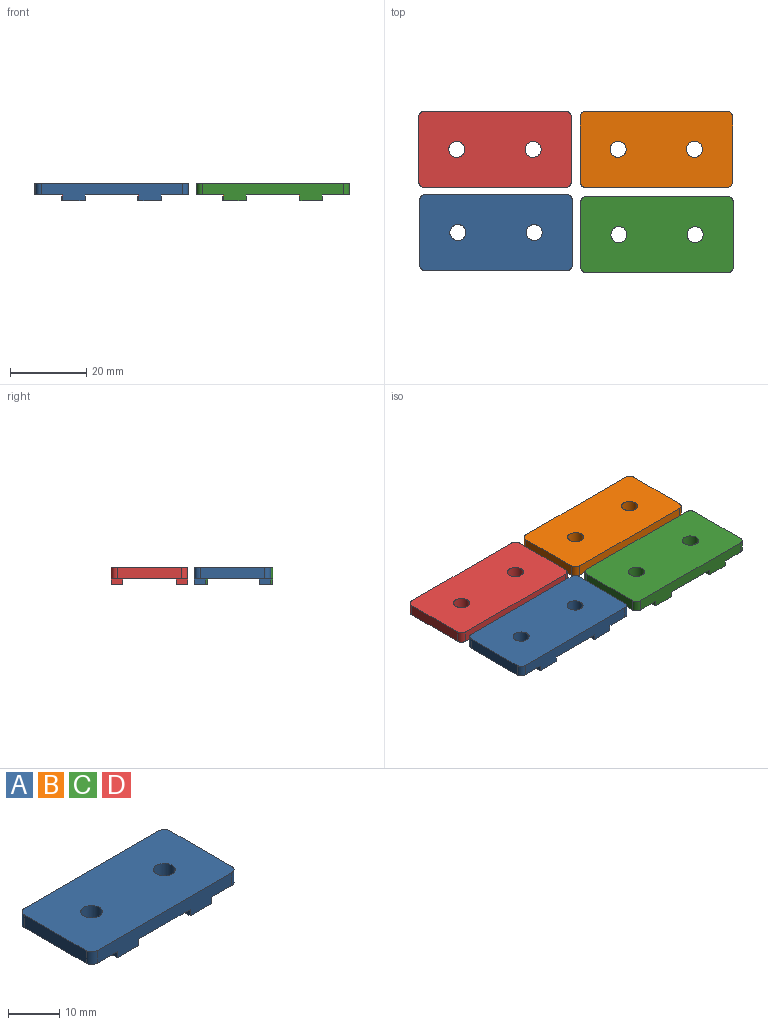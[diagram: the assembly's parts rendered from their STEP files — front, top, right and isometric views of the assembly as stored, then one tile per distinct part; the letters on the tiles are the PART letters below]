
ASSEMBLY  parts=4 mates=3
PART A: 28 faces, bbox 40x20x4.5 mm
  f0: plane 37x4.5mm, normal (0,-1,0), area 128.7mm2, adj f6,f7,f8,f11,f12,f13,f15,f24
  f1: plane 17x3mm, normal (1,0,0), area 51mm2, adj f6,f7,f8,f9
  f2: plane 37x4.5mm, normal (0,1,0), area 128.7mm2, adj f6,f7,f9,f10,f16,f17,f19,f20
  f3: cylinder r=2.1mm len=4.2mm, axis (0,0,-1), area 39.6mm2, adj f6,f7
  f4: cylinder r=2.1mm len=4.2mm, axis (0,0,-1), area 39.6mm2, adj f6,f7
  f5: plane 17x3mm, normal (-1,0,0), area 51mm2, adj f6,f7,f10,f11
  f6: plane 40x20mm, normal (0,0,1), area 770.4mm2, adj f0,f1,f2,f3,f4,f5,f8,f9
  f7: plane 40x20mm, normal (0,0,-1), area 700.2mm2, adj f0,f1,f2,f3,f4,f5,f8,f9
  f8: cylinder r=1.5mm len=3mm, axis (0,0,1), area 7.1mm2, adj f0,f1,f6,f7
  f9: cylinder r=1.5mm len=3mm, axis (0,0,-1), area 7.1mm2, adj f1,f2,f6,f7
  f10: cylinder r=1.5mm len=3mm, axis (0,0,1), area 7.1mm2, adj f2,f5,f6,f7
  f11: cylinder r=1.5mm len=3mm, axis (0,0,-1), area 7.1mm2, adj f0,f5,f6,f7
  f12: plane 3x1.5mm, normal (1,0,0), area 4.5mm2, adj f0,f7,f14,f15
  f13: plane 3x1.5mm, normal (-1,0,0), area 4.5mm2, adj f0,f7,f14,f15
  f14: plane 5.9x1.5mm, normal (0,1,0), area 8.8mm2, adj f7,f12,f13,f15
  f15: plane 5.9x3mm, normal (0,0,-1), area 17.7mm2, adj f0,f12,f13,f14
  f16: plane 3x1.5mm, normal (-1,0,0), area 4.5mm2, adj f2,f7,f18,f19
  f17: plane 3x1.5mm, normal (1,0,0), area 4.5mm2, adj f2,f7,f18,f19
  f18: plane 5.9x1.5mm, normal (0,-1,0), area 8.8mm2, adj f7,f16,f17,f19
  f19: plane 5.9x3mm, normal (0,0,-1), area 17.7mm2, adj f2,f16,f17,f18
  f20: plane 2.89x1.5mm, normal (-1,0,0), area 4.3mm2, adj f2,f7,f22,f23
  f21: plane 2.89x1.5mm, normal (1,0,0), area 4.3mm2, adj f2,f7,f22,f23
  f22: plane 5.9x1.5mm, normal (0,-1,0), area 8.8mm2, adj f7,f20,f21,f23
  f23: plane 5.9x2.89mm, normal (0,0,-1), area 17mm2, adj f2,f20,f21,f22
  f24: plane 3x1.5mm, normal (-1,0,0), area 4.5mm2, adj f0,f7,f25,f27
  f25: plane 5.9x1.5mm, normal (0,1,0), area 8.8mm2, adj f7,f24,f26,f27
  f26: plane 3x1.5mm, normal (1,0,0), area 4.5mm2, adj f0,f7,f25,f27
  f27: plane 5.9x3mm, normal (0,0,-1), area 17.7mm2, adj f0,f24,f25,f26
PART B: same geometry as A
PART C: same geometry as A
PART D: same geometry as A
PLACE A t=(-34.13,-1.32,-8.38)mm
PLACE B t=(7.89,20.5,-8.38)mm
PLACE C t=(8.09,-1.87,-8.38)mm
PLACE D t=(-34.42,20.47,-8.38)mm
MATE planar D.f6 <-> A.f6  axis (0,0,1) through (-34.42,10.47,-5.38)mm
MATE planar C.f6 <-> D.f6  axis (0,0,1) through (8.09,-11.87,-5.38)mm
MATE planar B.f6 <-> C.f6  axis (0,0,1) through (7.89,10.5,-5.38)mm
